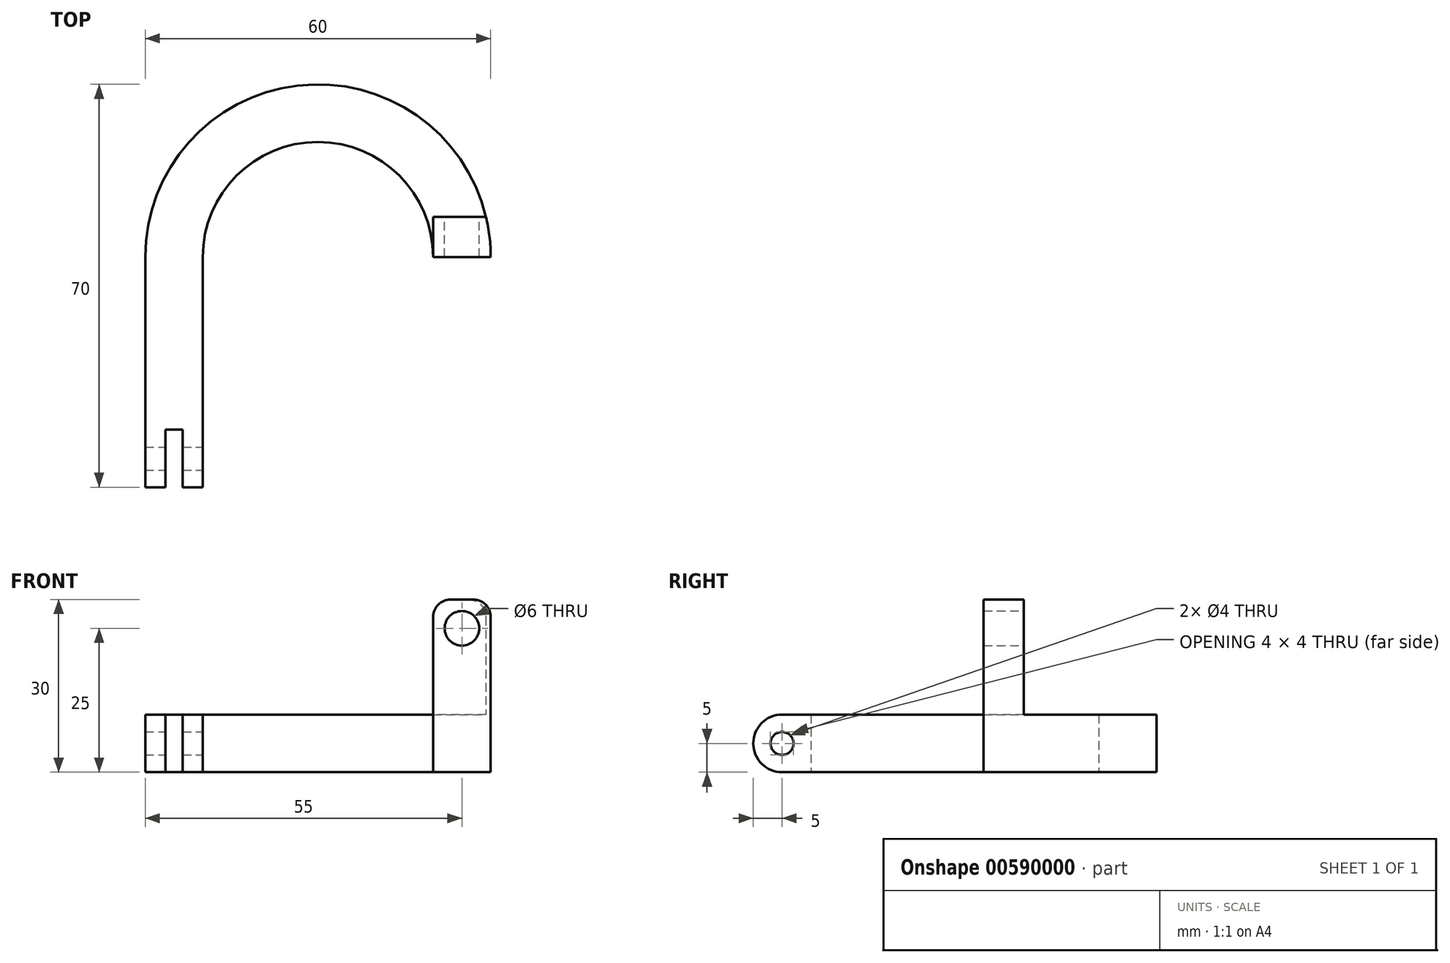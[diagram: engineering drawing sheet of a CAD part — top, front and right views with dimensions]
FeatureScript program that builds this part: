
annotation { "Feature Type Name" : "Feature", "Feature Type Description" : "" }
export const myFeature = defineFeature(function(context is Context, id is Id, definition is map)
    precondition{}
    {
        {
            var Q0;
            Q0=qCreatedBy(makeId("Top.planeOp"),FACE);
            var sketch = newSketch(context, id + "F0", { "sketchPlane" : qUnion([Q0])});
            skArc(sketch, "E0", {"start": v(25, 0) * mm, "mid": v(0, 25) * mm, "end": v(-25, 0) * mm, "construction": true});
            skArc(sketch, "E1", {"start": v(20, 0) * mm, "mid": v(0, 20) * mm, "end": v(-20, 0) * mm});
            skArc(sketch, "E2", {"start": v(30, 0) * mm, "mid": v(0, 30) * mm, "end": v(-30, 0) * mm});
            skLineSegment(sketch, "E3", {"start": v(-25, 0) * mm, "end": v(-25, -35) * mm, "construction": true});
            skLineSegment(sketch, "E4.bottom", {"start": v(-30, 0) * mm, "end": v(-20, 0) * mm, "construction": true});
            skLineSegment(sketch, "E4.top", {"start": v(-30, -40) * mm, "end": v(-26.5, -40) * mm});
            skLineSegment(sketch, "E4.left", {"start": v(-30, 0) * mm, "end": v(-30, -40) * mm});
            skLineSegment(sketch, "E4.right", {"start": v(-20, 0) * mm, "end": v(-20, -40) * mm});
            skLineSegment(sketch, "E5.top", {"start": v(-26.5, -30) * mm, "end": v(-23.5, -30) * mm});
            skLineSegment(sketch, "E5.left", {"start": v(-26.5, -40) * mm, "end": v(-26.5, -30) * mm});
            skLineSegment(sketch, "E5.right", {"start": v(-23.5, -40) * mm, "end": v(-23.5, -30) * mm});
            skLineSegment(sketch, "E6.trimOffspring", {"start": v(-23.5, -40) * mm, "end": v(-20, -40) * mm});
            skLineSegment(sketch, "E7", {"start": v(20, 0) * mm, "end": v(30, 0) * mm});
            skSolve(sketch);
        }
        {
            var Q0;
            Q0 = qSketchRegion(id + "F0", true);
            extrude(context, id + "F1", {"entities" : qUnion([Q0]), "depth" : 10 * mm, "offsetDistance" : 25 * mm});
        }
        {
            var Q0;
            Q0=makeQuery(id+"F1.opExtrude","CAP_EDGE",EDGE,{"disambiguationData":[OSD([sQuery(id+"F0.wireOp",EDGE,"E4.top")])],"isStart":false});
            var Q1;
            Q1=makeQuery(id+"F1.opExtrude","CAP_EDGE",EDGE,{"disambiguationData":[OSD([sQuery(id+"F0.wireOp",EDGE,"E4.top")])],"isStart":true});
            var Q2;
            Q2=makeQuery(id+"F1.opExtrude","CAP_EDGE",EDGE,{"disambiguationData":[OSD([sQuery(id+"F0.wireOp",EDGE,"E6.trimOffspring")])],"isStart":false});
            var Q3;
            Q3=makeQuery(id+"F1.opExtrude","CAP_EDGE",EDGE,{"disambiguationData":[OSD([sQuery(id+"F0.wireOp",EDGE,"E6.trimOffspring")])],"isStart":true});
            fillet(context, id + "F2", {"entities" : qUnion([Q0, Q1, Q2, Q3]), "radius" : 5 * mm, "tangentPropagation" : true, "allowEdgeOverflow" : false});
        }
        {
            var Q0;
            Q0=makeQuery(id+"F1.opExtrude","SWEPT_FACE",FACE,{"disambiguationData":[OSD([sQuery(id+"F0.wireOp",EDGE,"E4.right")])]});
            var sketch = newSketch(context, id + "F3", { "sketchPlane" : qUnion([Q0])});
            skCircle(sketch, "E8", {"center": v(-35, 5) * mm, "radius": 2 * mm});
            skSolve(sketch);
        }
        {
            var Q0;
            Q0 = qSketchRegion(id + "F3", true);
            extrude(context, id + "F4", {"entities" : qUnion([Q0]), "operationType" : NewBodyOperationType.REMOVE, "oppositeDirection" : true, "depth" : 25 * mm, "offsetDistance" : 25 * mm});
        }
        {
            var Q0;
            Q0=makeQuery(id+"F1.opExtrude","CAP_FACE",FACE,{"disambiguationData":[OSD([sQuery(id+"F0.wireOp",EDGE,"E1"),sQuery(id+"F0.wireOp",EDGE,"E2"),sQuery(id+"F0.wireOp",EDGE,"E4.top"),sQuery(id+"F0.wireOp",EDGE,"E4.left"),sQuery(id+"F0.wireOp",EDGE,"E4.right"),sQuery(id+"F0.wireOp",EDGE,"E5.top"),sQuery(id+"F0.wireOp",EDGE,"E5.left"),sQuery(id+"F0.wireOp",EDGE,"E5.right"),sQuery(id+"F0.wireOp",EDGE,"E6.trimOffspring"),sQuery(id+"F0.wireOp",EDGE,"E7")])],"isStart":true});
            var sketch = newSketch(context, id + "F5", { "sketchPlane" : qUnion([Q0])});
            skLineSegment(sketch, "E9.bottom", {"start": v(30, 0) * mm, "end": v(20, 0) * mm});
            skLineSegment(sketch, "E9.top", {"start": v(30, -7) * mm, "end": v(20, -7) * mm});
            skLineSegment(sketch, "E9.left", {"start": v(30, 0) * mm, "end": v(30, -7) * mm});
            skLineSegment(sketch, "E9.right", {"start": v(20, 0) * mm, "end": v(20, -7) * mm});
            skSolve(sketch);
        }
        {
            var Q0;
            {var subQ0=sQuery(id+"F5.wireOp",EDGE,"E9.bottom");Q0=makeQuery(id+"F5.imprint","IMPRINT",FACE,{"disambiguationData":[TD([[makeQuery(id+"F5.imprint","IMPRINT",EDGE,{"derivedFrom":subQ0}),-1.0]])]});}
            extrude(context, id + "F6", {"entities" : qUnion([Q0]), "operationType" : NewBodyOperationType.ADD, "oppositeDirection" : true, "depth" : 30 * mm, "offsetDistance" : 25 * mm});
        }
        {
            var Q0;
            Q0=makeQuery(id+"F6.opExtrude","CAP_EDGE",EDGE,{"disambiguationData":[OSD([sQuery(id+"F0.wireOp",EDGE,"E2")])],"isStart":false});
            var Q1;
            Q1=makeQuery(id+"F6.opExtrude","CAP_EDGE",EDGE,{"disambiguationData":[OSD([sQuery(id+"F5.wireOp",EDGE,"E9.right")])],"isStart":false});
            fillet(context, id + "F7", {"entities" : qUnion([Q0, Q1]), "radius" : 3 * mm, "tangentPropagation" : true, "allowEdgeOverflow" : false});
        }
        {
            var Q0;
            Q0=makeQuery(id+"F6.opExtrude","SWEPT_FACE",FACE,{"disambiguationData":[OSD([sQuery(id+"F5.wireOp",EDGE,"E9.top")])]});
            var sketch = newSketch(context, id + "F8", { "sketchPlane" : qUnion([Q0])});
            skCircle(sketch, "E10", {"center": v(-25, 25) * mm, "radius": 3 * mm});
            skSolve(sketch);
        }
        {
            var Q0;
            Q0 = qSketchRegion(id + "F8", true);
            extrude(context, id + "F9", {"entities" : qUnion([Q0]), "operationType" : NewBodyOperationType.REMOVE, "oppositeDirection" : true, "depth" : 25 * mm, "offsetDistance" : 25 * mm});
        }
    });
